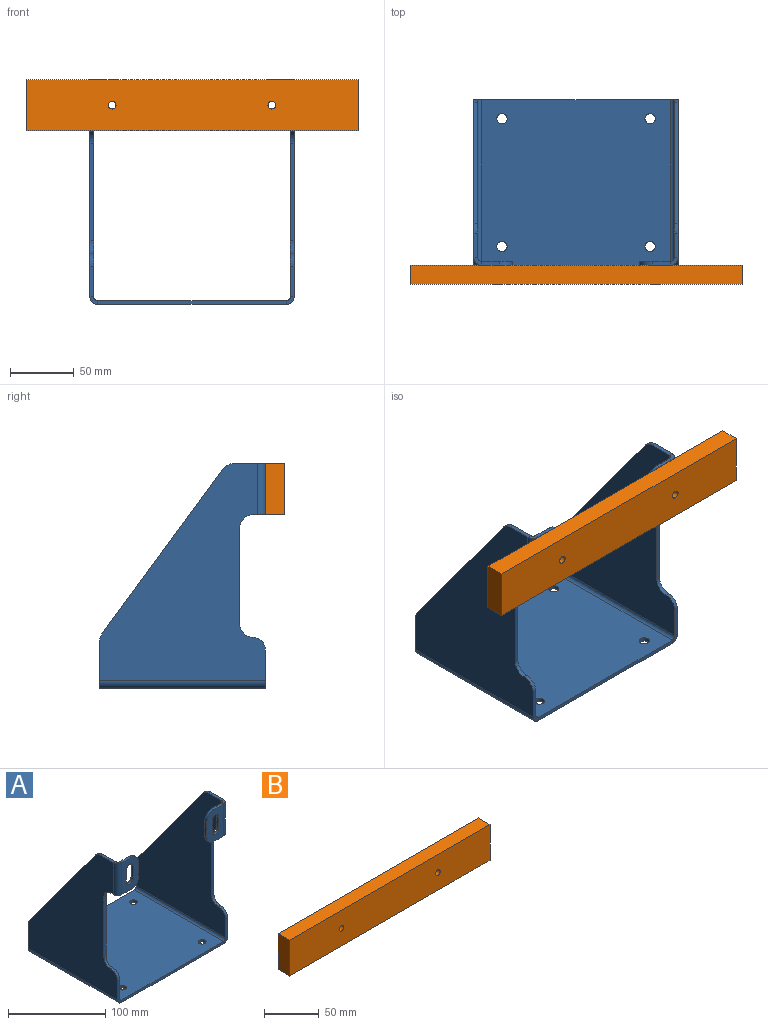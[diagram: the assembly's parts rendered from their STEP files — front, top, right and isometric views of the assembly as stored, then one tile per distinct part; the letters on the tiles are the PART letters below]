
ASSEMBLY  parts=2 mates=1
PART A: 72 faces, bbox 160x130x176 mm
  f0: plane 76x3mm, normal (0,-1,0), area 228mm2, adj f6,f7,f9,f12
  f1: plane 24x3mm, normal (0,-1,0), area 72mm2, adj f6,f7,f8,f54
  f2: plane 30.72x3mm, normal (0,1,0), area 92.2mm2, adj f6,f7,f10,f53
  f3: plane 129.28x95.06mm, normal (0,0.81,0.59), area 481.4mm2, adj f6,f7,f10,f11
  f4: plane 18.94x3mm, normal (0,0,1), area 56.8mm2, adj f6,f7,f11,f69
  f5: plane 4x3mm, normal (0,0,-1), area 12mm2, adj f6,f7,f12,f68
  f6: plane 170x130mm, normal (1,0,0), area 13156.6mm2, adj f0,f1,f2,f3,f4,f5,f8,f9
  f7: plane 170x130mm, normal (-1,0,0), area 13156.6mm2, adj f0,f1,f2,f3,f4,f5,f8,f9
  f8: cylinder r=10mm len=10mm, axis (-1,0,0), area 47.1mm2, adj f1,f6,f7,f9
  f9: cylinder r=10mm len=10mm, axis (1,0,0), area 47.1mm2, adj f0,f6,f7,f8
  f10: cylinder r=10mm len=5.92mm, axis (1,0,0), area 19mm2, adj f2,f3,f6,f7
  f11: cylinder r=10mm len=8.06mm, axis (1,0,0), area 28.1mm2, adj f3,f4,f6,f7
  f12: cylinder r=10mm len=10mm, axis (-1,0,0), area 47.1mm2, adj f0,f5,f6,f7
  f13: plane 148x3mm, normal (0,-1,0), area 444mm2, adj f19,f20,f50,f54
  f14: plane 148x3mm, normal (0,1,0), area 444mm2, adj f19,f20,f49,f53
  f15: cylinder r=4mm len=8mm, axis (0,0,1), area 75.4mm2, adj f19,f20
  f16: cylinder r=4mm len=8mm, axis (0,0,1), area 75.4mm2, adj f19,f20
  f17: cylinder r=4mm len=8mm, axis (0,0,1), area 75.4mm2, adj f19,f20
  f18: cylinder r=4mm len=8mm, axis (0,0,1), area 75.4mm2, adj f19,f20
  f19: plane 148x130mm, normal (0,0,1), area 19038.9mm2, adj f13,f14,f15,f16,f17,f18,f52,f56
  f20: plane 148x130mm, normal (0,0,-1), area 19038.9mm2, adj f13,f14,f15,f16,f17,f18,f51,f55
  f21: plane 18.94x3mm, normal (0,0,1), area 56.8mm2, adj f27,f28,f33,f45
  f22: plane 129.28x95.06mm, normal (0,0.81,0.59), area 481.4mm2, adj f27,f28,f32,f33
  f23: plane 30.72x3mm, normal (0,1,0), area 92.2mm2, adj f27,f28,f32,f49
  f24: plane 24x3mm, normal (0,-1,0), area 72mm2, adj f27,f28,f30,f50
  f25: plane 76x3mm, normal (0,-1,0), area 228mm2, adj f27,f28,f29,f31
  f26: plane 4x3mm, normal (0,0,-1), area 12mm2, adj f27,f28,f31,f46
  f27: plane 170x130mm, normal (-1,0,0), area 13156.6mm2, adj f21,f22,f23,f24,f25,f26,f29,f30
  f28: plane 170x130mm, normal (1,0,0), area 13156.6mm2, adj f21,f22,f23,f24,f25,f26,f29,f30
  f29: cylinder r=10mm len=10mm, axis (-1,0,0), area 47.1mm2, adj f25,f27,f28,f30
  f30: cylinder r=10mm len=10mm, axis (1,0,0), area 47.1mm2, adj f24,f27,f28,f29
  f31: cylinder r=10mm len=10mm, axis (1,0,0), area 47.1mm2, adj f25,f26,f27,f28
  f32: cylinder r=10mm len=5.92mm, axis (-1,0,0), area 19mm2, adj f22,f23,f27,f28
  f33: cylinder r=10mm len=8.06mm, axis (1,0,0), area 28.1mm2, adj f21,f22,f27,f28
  f34: cylinder r=5mm len=10mm, axis (0,1,0), area 47.1mm2, adj f35,f40,f41,f42
  f35: plane 15x3mm, normal (1,0,0), area 45mm2, adj f34,f36,f41,f42
  f36: cylinder r=5mm len=10mm, axis (0,1,0), area 47.1mm2, adj f35,f40,f41,f42
  f37: plane 20x3mm, normal (-1,0,0), area 60mm2, adj f41,f42,f43,f44
  f38: plane 14x3mm, normal (0,0,1), area 42mm2, adj f41,f42,f44,f45
  f39: plane 14x3mm, normal (0,0,-1), area 42mm2, adj f41,f42,f43,f46
  f40: plane 15x3mm, normal (-1,0,0), area 45mm2, adj f34,f36,f41,f42
  f41: plane 40x24mm, normal (0,1,0), area 688.5mm2, adj f34,f35,f36,f37,f38,f39,f40,f43
  f42: plane 40x24mm, normal (0,-1,0), area 688.5mm2, adj f34,f35,f36,f37,f38,f39,f40,f43
  f43: cylinder r=10mm len=10mm, axis (0,1,0), area 47.1mm2, adj f37,f39,f41,f42
  f44: cylinder r=10mm len=10mm, axis (0,1,0), area 47.1mm2, adj f37,f38,f41,f42
  f45: plane 6x6mm, normal (0,0,1), area 21.2mm2, adj f21,f38,f47,f48
  f46: plane 6x6mm, normal (0,0,-1), area 21.2mm2, adj f26,f39,f47,f48
  f47: cylinder r=6mm len=40mm, axis (0,0,1), area 377mm2, adj f28,f42,f45,f46
  f48: cylinder r=3mm len=40mm, axis (0,0,1), area 188.5mm2, adj f27,f41,f45,f46
  f49: plane 6x6mm, normal (0,1,0), area 21.2mm2, adj f14,f23,f51,f52
  f50: plane 6x6mm, normal (0,-1,0), area 21.2mm2, adj f13,f24,f51,f52
  f51: cylinder r=6mm len=130mm, axis (0,1,0), area 1225.2mm2, adj f20,f28,f49,f50
  f52: cylinder r=3mm len=130mm, axis (0,1,0), area 612.6mm2, adj f19,f27,f49,f50
  f53: plane 6x6mm, normal (0,1,0), area 21.2mm2, adj f2,f14,f55,f56
  f54: plane 6x6mm, normal (0,-1,0), area 21.2mm2, adj f1,f13,f55,f56
  f55: cylinder r=6mm len=130mm, axis (0,1,0), area 1225.2mm2, adj f7,f20,f53,f54
  f56: cylinder r=3mm len=130mm, axis (0,1,0), area 612.6mm2, adj f6,f19,f53,f54
  f57: cylinder r=5mm len=10mm, axis (0,1,0), area 47.1mm2, adj f58,f63,f64,f65
  f58: plane 15x3mm, normal (1,0,0), area 45mm2, adj f57,f59,f64,f65
  f59: cylinder r=5mm len=10mm, axis (0,1,0), area 47.1mm2, adj f58,f63,f64,f65
  f60: plane 20x3mm, normal (1,0,0), area 60mm2, adj f64,f65,f66,f67
  f61: plane 14x3mm, normal (0,0,-1), area 42mm2, adj f64,f65,f66,f68
  f62: plane 14x3mm, normal (0,0,1), area 42mm2, adj f64,f65,f67,f69
  f63: plane 15x3mm, normal (-1,0,0), area 45mm2, adj f57,f59,f64,f65
  f64: plane 40x24mm, normal (0,1,0), area 688.5mm2, adj f57,f58,f59,f60,f61,f62,f63,f66
  f65: plane 40x24mm, normal (0,-1,0), area 688.5mm2, adj f57,f58,f59,f60,f61,f62,f63,f66
  f66: cylinder r=10mm len=10mm, axis (0,1,0), area 47.1mm2, adj f60,f61,f64,f65
  f67: cylinder r=10mm len=10mm, axis (0,1,0), area 47.1mm2, adj f60,f62,f64,f65
  f68: plane 6x6mm, normal (0,0,-1), area 21.2mm2, adj f5,f61,f70,f71
  f69: plane 6x6mm, normal (0,0,1), area 21.2mm2, adj f4,f62,f70,f71
  f70: cylinder r=6mm len=40mm, axis (0,0,-1), area 377mm2, adj f7,f65,f68,f69
  f71: cylinder r=3mm len=40mm, axis (0,0,-1), area 188.5mm2, adj f6,f64,f68,f69
PART B: 8 faces, bbox 260x15x40 mm
  f0: plane 40x15mm, normal (1,0,0), area 600mm2, adj f1,f3,f4,f5
  f1: plane 260x15mm, normal (0,0,1), area 3900mm2, adj f0,f2,f4,f5
  f2: plane 40x15mm, normal (-1,0,0), area 600mm2, adj f1,f3,f4,f5
  f3: plane 260x15mm, normal (0,0,-1), area 3900mm2, adj f0,f2,f4,f5
  f4: plane 260x40mm, normal (0,-1,0), area 10343.5mm2, adj f0,f1,f2,f3,f6,f7
  f5: plane 260x40mm, normal (0,1,0), area 10343.5mm2, adj f0,f1,f2,f3,f6,f7
  f6: cylinder r=3mm len=15mm, axis (0,1,0), area 282.7mm2, adj f4,f5
  f7: cylinder r=3mm len=15mm, axis (0,1,0), area 282.7mm2, adj f4,f5
PLACE A at identity fixed
PLACE B t=(0,0,156)mm
MATE planar B.f7 <-> A.f42  axis (0,1,0) through (62.5,0,156)mm
